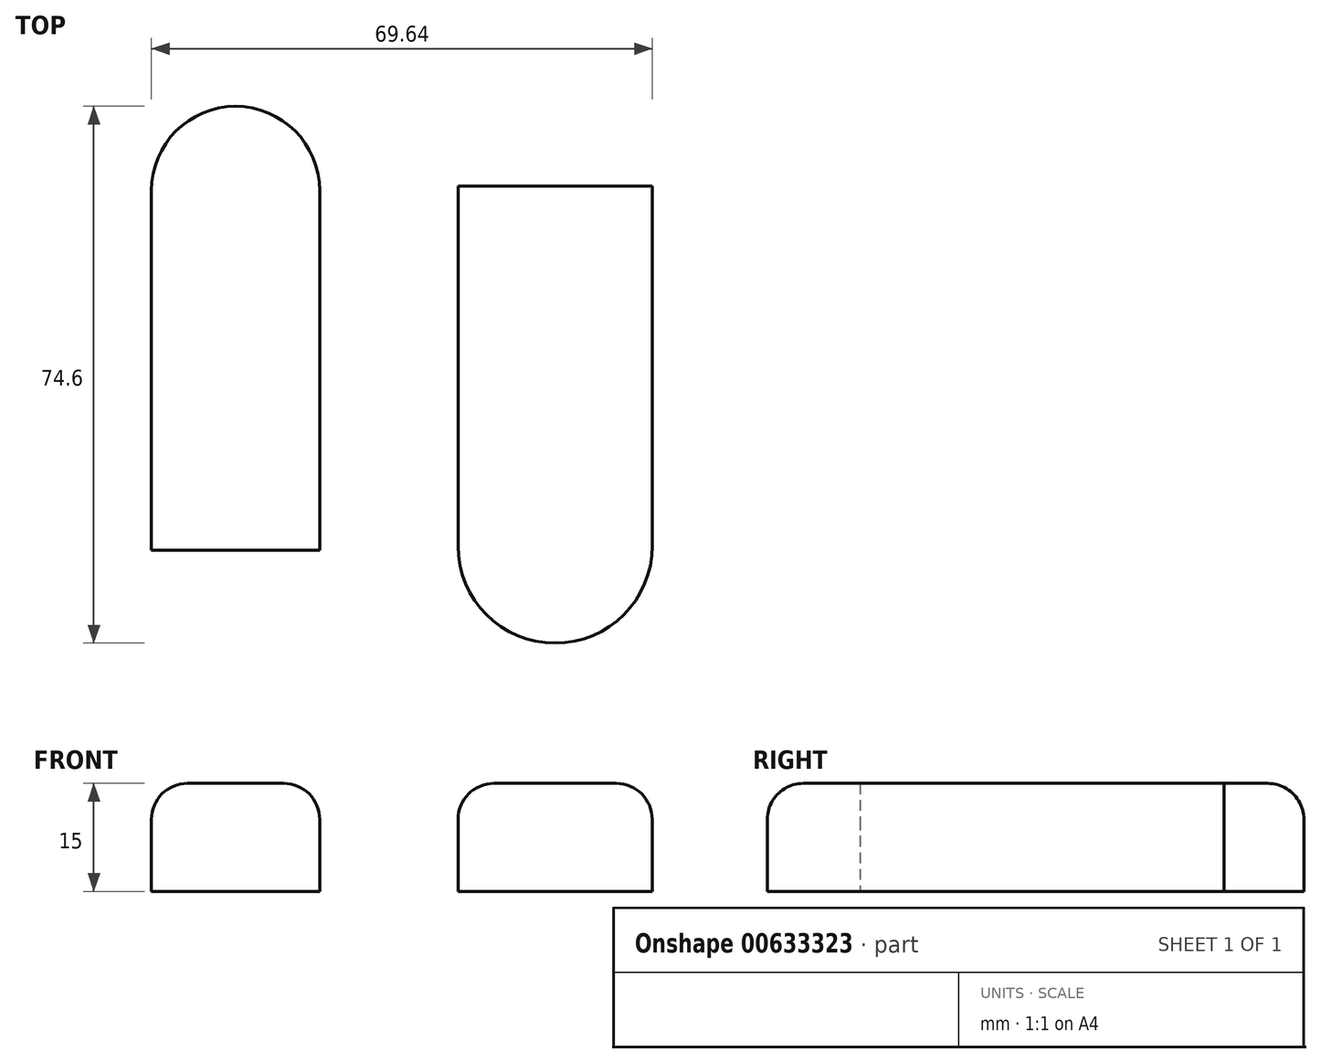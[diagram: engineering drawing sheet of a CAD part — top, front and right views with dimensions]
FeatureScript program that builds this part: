
annotation { "Feature Type Name" : "Feature", "Feature Type Description" : "" }
export const myFeature = defineFeature(function(context is Context, id is Id, definition is map)
    precondition{}
    {
        {
            var Q0;
            Q0=qCreatedBy(makeId("Top.planeOp"),FACE);
            var sketch = newSketch(context, id + "F0", { "sketchPlane" : qUnion([Q0])});
            skLineSegment(sketch, "E0", {"start": v(-13.77, 21.13) * mm, "end": v(-13.77, -28.87) * mm});
            skLineSegment(sketch, "E1", {"start": v(9.62, 21.13) * mm, "end": v(9.62, -28.87) * mm});
            skArc(sketch, "E2", {"start": v(9.62, 21.13) * mm, "mid": v(-2.07, 32.83) * mm, "end": v(-13.77, 21.13) * mm});
            skLineSegment(sketch, "E3", {"start": v(-13.77, -28.87) * mm, "end": v(9.62, -28.87) * mm});
            skSolve(sketch);
        }
        {
            var Q0;
            Q0=makeQuery(id+"F0.imprint","IMPRINT",FACE,{"disambiguationData":[TD([[makeQuery(id+"F0.imprint","IMPRINT",EDGE,{"derivedFrom":sQuery(id+"F0.wireOp",EDGE,"E0")}),1.0]])]});
            extrude(context, id + "F1", {"entities" : qUnion([Q0]), "depth" : 15 * mm, "offsetDistance" : 25 * mm});
        }
        {
            var Q0;
            Q0=qCreatedBy(makeId("Top.planeOp"),FACE);
            var sketch = newSketch(context, id + "F2", { "sketchPlane" : qUnion([Q0])});
            skLineSegment(sketch, "E4", {"start": v(28.87, 21.73) * mm, "end": v(28.87, -28.27) * mm});
            skLineSegment(sketch, "E5", {"start": v(55.87, 21.73) * mm, "end": v(55.87, -28.27) * mm});
            skLineSegment(sketch, "E6", {"start": v(28.87, 21.73) * mm, "end": v(48.87, 21.73) * mm});
            skLineSegment(sketch, "E7", {"start": v(48.87, 21.73) * mm, "end": v(55.87, 21.73) * mm});
            skArc(sketch, "E8", {"start": v(28.87, -28.27) * mm, "mid": v(42.37, -41.77) * mm, "end": v(55.87, -28.27) * mm});
            skSolve(sketch);
        }
        {
            var Q0;
            Q0=makeQuery(id+"F2.imprint","IMPRINT",FACE,{"disambiguationData":[TD([[makeQuery(id+"F2.imprint","IMPRINT",EDGE,{"derivedFrom":sQuery(id+"F2.wireOp",EDGE,"E4")}),1.0]])]});
            extrude(context, id + "F3", {"entities" : qUnion([Q0]), "depth" : 15 * mm, "offsetDistance" : 25 * mm});
        }
        {
            var Q0;
            Q0=makeQuery(id+"F1.opExtrude","CAP_EDGE",EDGE,{"disambiguationData":[OSD([sQuery(id+"F0.wireOp",EDGE,"E0")])],"isStart":false});
            var Q1;
            Q1=makeQuery(id+"F3.opExtrude","CAP_EDGE",EDGE,{"disambiguationData":[OSD([sQuery(id+"F2.wireOp",EDGE,"E4")])],"isStart":false});
            fillet(context, id + "F4", {"entities" : qUnion([Q0, Q1]), "radius" : 5 * mm, "tangentPropagation" : true, "allowEdgeOverflow" : false});
        }
    });
